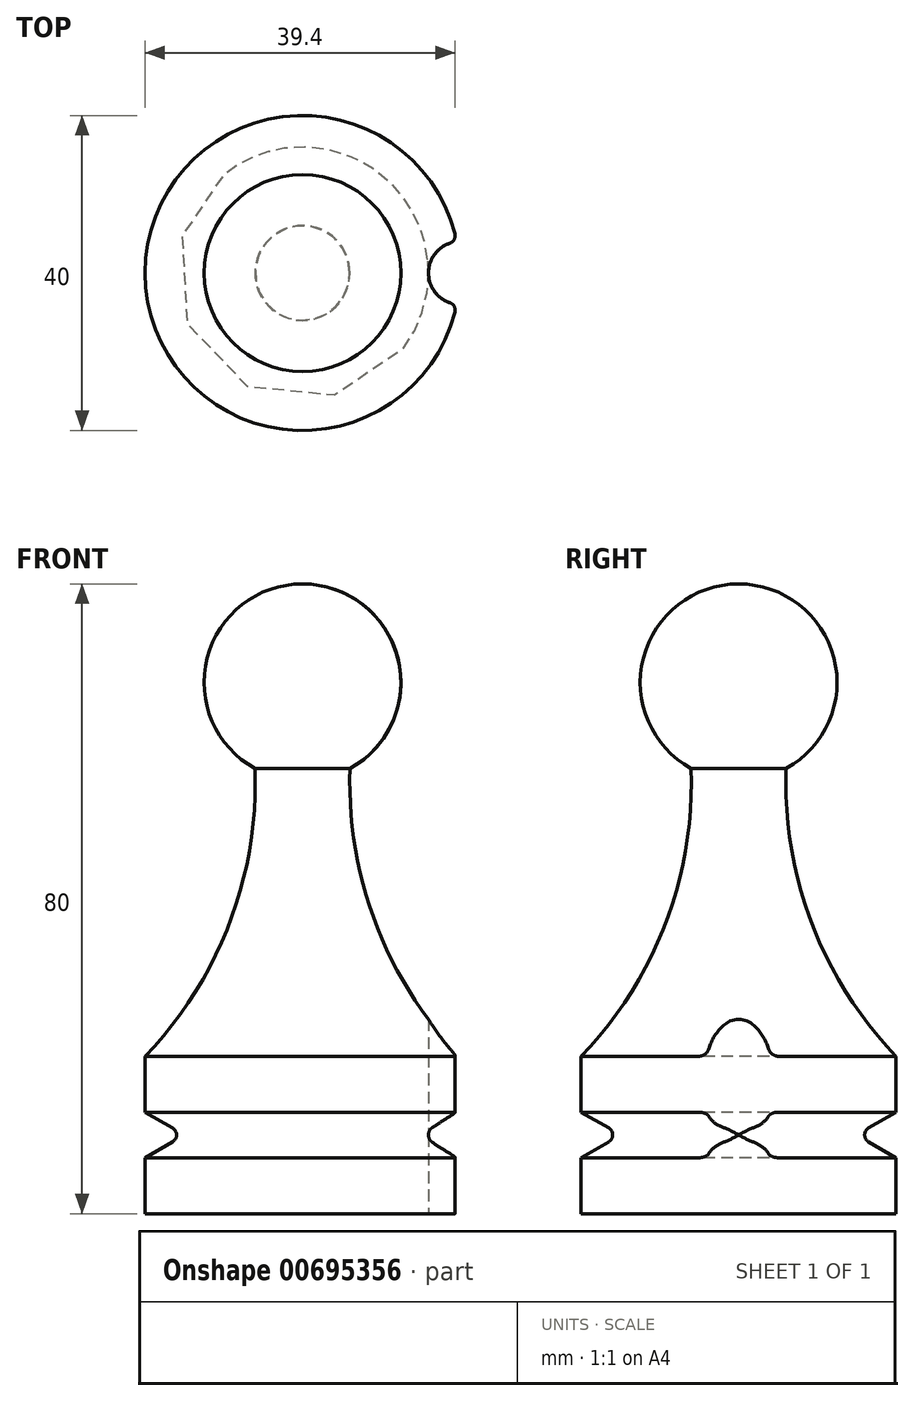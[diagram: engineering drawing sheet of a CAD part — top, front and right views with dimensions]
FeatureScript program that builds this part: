
annotation { "Feature Type Name" : "Feature", "Feature Type Description" : "" }
export const myFeature = defineFeature(function(context is Context, id is Id, definition is map)
    precondition{}
    {
        {
            var Q0;
            Q0=qCreatedBy(makeId("Front.planeOp"),FACE);
            var sketch = newSketch(context, id + "F0", { "sketchPlane" : qUnion([Q0])});
            skLineSegment(sketch, "E0", {"start": v(0, 73.5) * mm, "end": v(0, -42.64) * mm, "construction": true});
            skLineSegment(sketch, "E1", {"start": v(0, 0) * mm, "end": v(20, 0) * mm});
            skLineSegment(sketch, "E2", {"start": v(20, 0) * mm, "end": v(20, 12.89) * mm});
            skLineSegment(sketch, "E3", {"start": v(20, 12.89) * mm, "end": v(15, 10) * mm});
            skLineSegment(sketch, "E4", {"start": v(15, 10) * mm, "end": v(20, 7.11) * mm});
            skPoint(sketch, "E4.endSnap0", {"position": v(20, 6.44) * mm});
            skLineSegment(sketch, "E5", {"start": v(20, 7.11) * mm, "end": v(20, 20) * mm});
            skArc(sketch, "E6", {"start": v(6.03, 56.55) * mm, "mid": v(9.3, 36.85) * mm, "end": v(20, 20) * mm});
            skArc(sketch, "E7", {"start": v(6.03, 56.55) * mm, "mid": v(12.1, 70.62) * mm, "end": v(0, 80) * mm});
            skLineSegment(sketch, "E8", {"start": v(0, 80) * mm, "end": v(0, 0) * mm});
            skSolve(sketch);
        }
        {
            var Q0;
            Q0=makeQuery(id+"F0.imprint","IMPRINT",FACE,{"disambiguationData":[TD([[makeQuery(id+"F0.imprint","IMPRINT",EDGE,{"derivedFrom":sQuery(id+"F0.wireOp",EDGE,"E1")}),1.0]])]});
            var Q1;
            Q1=sQuery(id+"F0.wireOp",EDGE,"E8");
            revolve(context, id + "F1", {"surfaceOperationType" : NewSurfaceOperationType.NEW, "entities" : qUnion([Q0]), "axis" : qUnion([Q1]), "revolveType" : RevolveType.FULL});
        }
        {
            var Q0;
            Q0=makeQuery(id+"F1.opRevolve","SWEPT_FACE",FACE,{"disambiguationData":[OSD([sQuery(id+"F0.wireOp",EDGE,"E1")])]});
            var sketch = newSketch(context, id + "F2", { "sketchPlane" : qUnion([Q0])});
            skCircle(sketch, "E9", {"center": v(20, 0) * mm, "radius": 4 * mm});
            skSolve(sketch);
        }
        {
            var Q0;
            {var subQ0=sQuery(id+"F2.wireOp",EDGE,"E9");var subQ1=makeQuery(id+"F1.opRevolve","SWEPT_EDGE",EDGE,{"disambiguationData":[OSD([sQuery(id+"F0.wireOp",EDGE,"E1"),sQuery(id+"F0.wireOp",EDGE,"E2")])]});var subQ2=makeQuery(id+"F2.imprint","INTERSECT",VERTEX,{"disambiguationData":[OD(0.0)],"derivedFrom":[subQ1,subQ0]});Q0=makeQuery(id+"F2.imprint","IMPRINT",FACE,{"disambiguationData":[TD([[makeQuery(id+"F2.imprint","IMPRINT",EDGE,{"disambiguationData":[TD([[subQ2,1.0]])],"derivedFrom":subQ0}),1.0]])]});}
            var Q1;
            {var subQ0=sQuery(id+"F2.wireOp",EDGE,"E9");var subQ1=makeQuery(id+"F1.opRevolve","SWEPT_EDGE",EDGE,{"disambiguationData":[OSD([sQuery(id+"F0.wireOp",EDGE,"E1"),sQuery(id+"F0.wireOp",EDGE,"E2")])]});var subQ2=makeQuery(id+"F2.imprint","INTERSECT",VERTEX,{"disambiguationData":[OD(0.0)],"derivedFrom":[subQ1,subQ0]});Q1=makeQuery(id+"F2.imprint","IMPRINT",FACE,{"disambiguationData":[TD([[makeQuery(id+"F2.imprint","IMPRINT",EDGE,{"disambiguationData":[TD([[subQ2,-1.0]])],"derivedFrom":subQ0}),1.0]])]});}
            extrude(context, id + "F3", {"entities" : qUnion([Q0, Q1]), "operationType" : NewBodyOperationType.REMOVE, "oppositeDirection" : true, "depth" : 25 * mm, "offsetDistance" : 25 * mm});
        }
        {
            var Q0;
            Q0=makeQuery(id+"F3.boolean.opBoolean","INTERSECT",EDGE,{"disambiguationData":[OD(0.0)],"derivedFrom":[makeQuery(id+"F1.opRevolve","SWEPT_FACE",FACE,{"disambiguationData":[OSD([sQuery(id+"F0.wireOp",EDGE,"E5")])]}),makeQuery(id+"F3.opExtrude","SWEPT_FACE",FACE,{"disambiguationData":[OSD([sQuery(id+"F2.wireOp",EDGE,"E9")])]})]});
            var Q1;
            Q1=makeQuery(id+"F3.boolean.opBoolean","INTERSECT",EDGE,{"disambiguationData":[OD(1.0)],"derivedFrom":[makeQuery(id+"F1.opRevolve","SWEPT_FACE",FACE,{"disambiguationData":[OSD([sQuery(id+"F0.wireOp",EDGE,"E5")])]}),makeQuery(id+"F3.opExtrude","SWEPT_FACE",FACE,{"disambiguationData":[OSD([sQuery(id+"F2.wireOp",EDGE,"E9")])]})]});
            var Q2;
            Q2=makeQuery(id+"F3.boolean.opBoolean","INTERSECT",EDGE,{"disambiguationData":[OD(0.0)],"derivedFrom":[makeQuery(id+"F1.opRevolve","SWEPT_FACE",FACE,{"disambiguationData":[OSD([sQuery(id+"F0.wireOp",EDGE,"E2")])]}),makeQuery(id+"F3.opExtrude","SWEPT_FACE",FACE,{"disambiguationData":[OSD([sQuery(id+"F2.wireOp",EDGE,"E9")])]})]});
            var Q3;
            Q3=makeQuery(id+"F3.boolean.opBoolean","INTERSECT",EDGE,{"disambiguationData":[OD(1.0)],"derivedFrom":[makeQuery(id+"F1.opRevolve","SWEPT_FACE",FACE,{"disambiguationData":[OSD([sQuery(id+"F0.wireOp",EDGE,"E2")])]}),makeQuery(id+"F3.opExtrude","SWEPT_FACE",FACE,{"disambiguationData":[OSD([sQuery(id+"F2.wireOp",EDGE,"E9")])]})]});
            fillet(context, id + "F4", {"entities" : qUnion([Q0, Q1, Q2, Q3]), "radius" : 1 * mm, "tangentPropagation" : true, "allowEdgeOverflow" : false});
        }
        {
            var Q0;
            Q0=makeQuery(id+"F1.opRevolve","SWEPT_EDGE",EDGE,{"disambiguationData":[OSD([sQuery(id+"F0.wireOp",EDGE,"E3"),sQuery(id+"F0.wireOp",EDGE,"E4")])]});
            fillet(context, id + "F5", {"entities" : qUnion([Q0]), "radius" : 1 * mm, "tangentPropagation" : true, "allowEdgeOverflow" : false});
        }
    });
